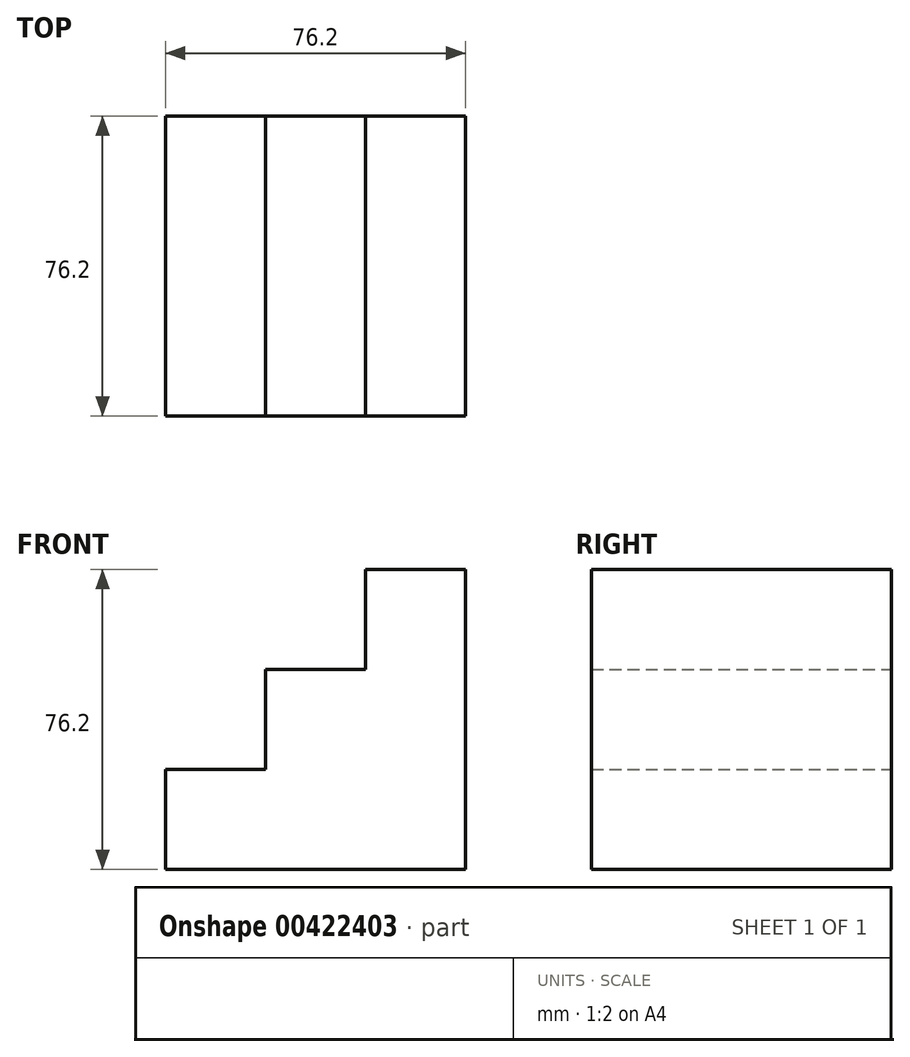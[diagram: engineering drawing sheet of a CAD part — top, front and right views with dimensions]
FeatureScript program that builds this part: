
annotation { "Feature Type Name" : "Feature", "Feature Type Description" : "" }
export const myFeature = defineFeature(function(context is Context, id is Id, definition is map)
    precondition{}
    {
        {
            var Q0;
            Q0=qCreatedBy(makeId("Front.planeOp"),FACE);
            var sketch = newSketch(context, id + "F0", { "sketchPlane" : qUnion([Q0])});
            skLineSegment(sketch, "E0", {"start": v(-69.6, -50.68) * mm, "end": v(6.6, -50.68) * mm});
            skLineSegment(sketch, "E1", {"start": v(6.6, -50.68) * mm, "end": v(6.6, 25.52) * mm});
            skLineSegment(sketch, "E2", {"start": v(6.6, 25.52) * mm, "end": v(-18.8, 25.52) * mm});
            skLineSegment(sketch, "E3", {"start": v(-18.8, 25.52) * mm, "end": v(-18.8, 0.12) * mm});
            skLineSegment(sketch, "E4", {"start": v(-18.8, 0.12) * mm, "end": v(-44.2, 0.12) * mm});
            skLineSegment(sketch, "E5", {"start": v(-44.2, 0.12) * mm, "end": v(-44.2, -25.28) * mm});
            skLineSegment(sketch, "E6", {"start": v(-44.2, -25.28) * mm, "end": v(-69.6, -25.28) * mm});
            skLineSegment(sketch, "E7", {"start": v(-69.6, -25.28) * mm, "end": v(-69.6, -50.68) * mm});
            skSolve(sketch);
        }
        {
            var Q0;
            Q0=makeQuery(id+"F0.imprint","IMPRINT",FACE,{"disambiguationData":[TD([[makeQuery(id+"F0.imprint","IMPRINT",EDGE,{"derivedFrom":sQuery(id+"F0.wireOp",EDGE,"E0")}),1.0]])]});
            extrude(context, id + "F1", {"entities" : qUnion([Q0]), "depth" : 76.2 * mm});
        }
    });
